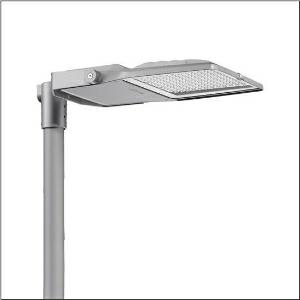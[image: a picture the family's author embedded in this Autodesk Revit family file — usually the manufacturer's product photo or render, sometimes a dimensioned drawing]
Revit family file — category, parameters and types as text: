
# Revit family: floodlight_fl_21_iq_midi___pl64_5xa7781e4e3a_69c6
name_source: partatom
category: Lighting Fixtures
units: mm (PartAtom-declared; Revit-internal decimal feet)

## family parameters
Cut with Voids When Loaded = No
Host = Face
Light Source = No
Part Type = Normal
Room Calculation Point = No
Round Connector Dimension = Use Diameter
Shared = No

## types (1)
- --- (1 x LED, 27050 lm, 208.1 W, 4000K)
    Apparent Load = 208 VA
    CIE Flux Codes = 28 80 98 100 100
    Color Rendering = 70
    Color Temperature = 4000K
    Default Elevation = 1800 mm
    Description = Floodlight FL 21 iQ midi, floodlight, primary light control with lens, of PMMA, primary optical cover: protective disc, of toughened safety glass, transparent, light distribution: PL64, light emission: direct distribution, installation type: surface-mounted, lamps: LED, High Power LED, rated values: 27.050lm | 208,1W | 130lm/W (begin service life); end service life: 27.050lm | 227,1W; at 50% lumin. flux: 13.525lm | 90,3W | 149,8lm/W, colour temperature: 4000K, colour rendering: CRI > 70, light colour: 740, light setting 1 begin service life: 100% | 27.050lm | 208,1W | 130lm/W | 4.000K, light setting 1 end service life: 227,1W, further light settings possible, control: optimised constant luminous flux control (CLO 2.0), Desk-Remote (wireless, voltage-free reading and setting of iQ features in the workshop via application-optimized NFC function/RFID function), Light-Fading, Smart-Wire, Night-Set, Lumen-Switch, Temp-Guard, Auto-Match, pre-setting: linear dimming characteristic, with terminal, 6-pole, mains connection: 220..240V, AC, 50/60Hz, luminaire housing, of diecast aluminium, powder-coated, SITECO metallic grey (DB 702S), corrosivity category C5 mid according to DIN EN ISO 12944suitable for swimming poolschlorine-resistant, sealing non-destructively replaceable, please order mast flange separately, mast bracket, of steel, galvanised, powder-coated, SITECO metallic grey (DB 702S), protection rating (complete): IP66, insulation class (complete): insulation class II (safety insulation), certification: CE, ENEC, VDE, protection symbol: D, impact resistance: IK08, permissible operating ambient temperature: -40..+40°C, permissible operating ambient temperature for outdoor applications: -40..+50°C, standard: DIN EN 12944, LABS conformity tested according to VDMA 24364:2018-05, packaging unit: 1 piece

Light Distribution: PL64
    Height = 76 mm
    Lamp = 1 x LED
    Lamp Light Flux = 27050 lm
    Lamp Power = 208.1 W
    Lamp count = 1
    Length = 657 mm
    Luminous efficacy = 130 lm/W
    Manufacturer = Siteco
    ModVariant = No
    Model = 5XA7781E4E3A
    Number of Poles = 1
    OnlyDefault = Yes
    Power Factor = 1
    Product Name = Floodlight FL 21 iQ midi | PL64
    Product group = floodlight | pylon annexe
    ProductGroupID = 6201
    Protection Class = Protection class II
    Protection Degree = IP 66
    RLX_Detail_Level = 1
    RLX_Emergency_Light_Flux = 0 lm
    RLX_Emergency_Type = 0
    RLX_Emergency_Type_DB = No
    RlxData = <blob elided: 153869 chars, md5=6c90b377>
    Socket = socket
    Standby Power = 0 W
    System Light Flux = 27050 lm
    System Power = 208 W
    Type Comments = factory setting: luminous flux: 100 % | dim-lin: 254 | 710 mA
    Type Image = l_1007123.jpg
    URL = http://relux.com
    VarID = @adj_107155
    Voltage = 0 V
    Weight = 0.00 kg
    Width = 442 mm

## geometry (parser evidence)
native form markers: Blend x4, Sweep x15
no freeform markers — native parametric forms only
